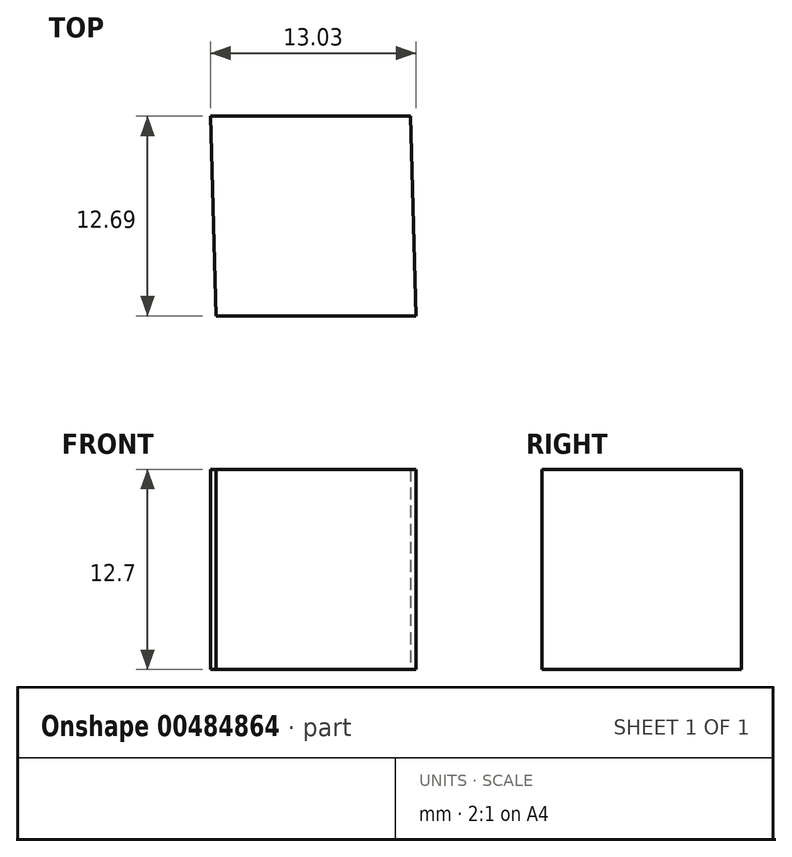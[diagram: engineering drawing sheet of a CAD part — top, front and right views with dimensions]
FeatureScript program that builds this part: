
annotation { "Feature Type Name" : "Feature", "Feature Type Description" : "" }
export const myFeature = defineFeature(function(context is Context, id is Id, definition is map)
    precondition{}
    {
        {
            var Q0;
            Q0=qCreatedBy(makeId("Top.planeOp"),FACE);
            var sketch = newSketch(context, id + "F0", { "sketchPlane" : qUnion([Q0])});
            skLineSegment(sketch, "E0", {"start": v(-121.18, -6.8) * mm, "end": v(-108.48, -6.8) * mm});
            skLineSegment(sketch, "E1", {"start": v(-108.48, -6.8) * mm, "end": v(-108.15, -19.5) * mm});
            skLineSegment(sketch, "E2", {"start": v(-108.15, -19.5) * mm, "end": v(-120.85, -19.5) * mm});
            skLineSegment(sketch, "E3", {"start": v(-120.85, -19.5) * mm, "end": v(-121.18, -6.8) * mm});
            skSolve(sketch);
        }
        {
            var Q0;
            Q0 = qSketchRegion(id + "F0", true);
            extrude(context, id + "F1", {"entities" : qUnion([Q0]), "depth" : 12.7 * mm});
        }
    });
